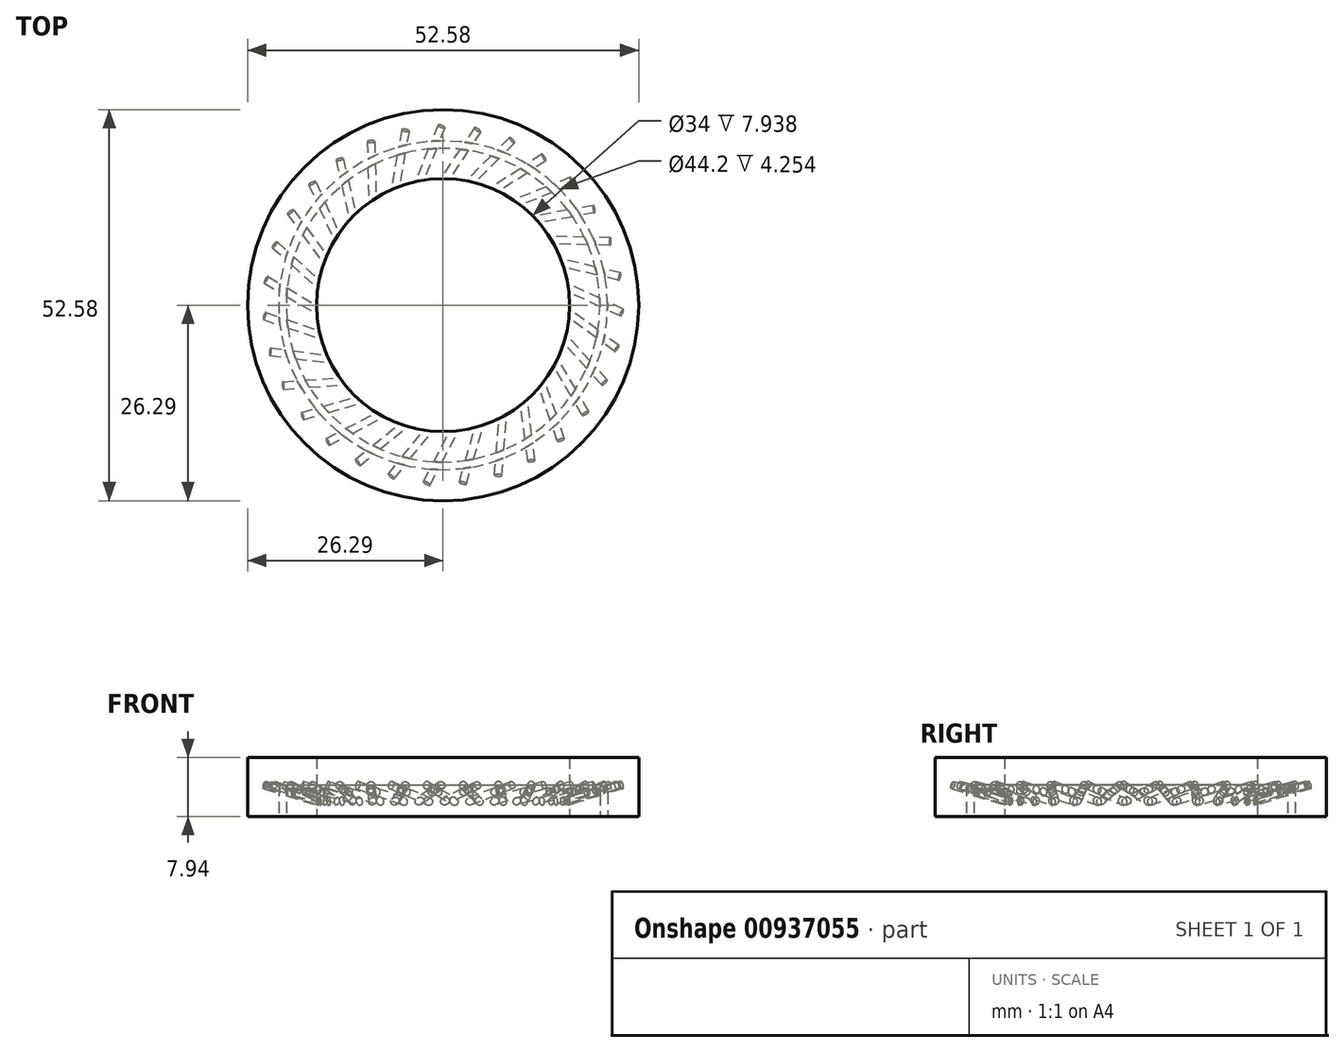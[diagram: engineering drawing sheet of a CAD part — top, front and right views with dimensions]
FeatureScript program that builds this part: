
annotation { "Feature Type Name" : "Feature", "Feature Type Description" : "" }
export const myFeature = defineFeature(function(context is Context, id is Id, definition is map)
    precondition{}
    {
        {
            var Q0;
            Q0=qCreatedBy(makeId("Top.planeOp"),FACE);
            var sketch = newSketch(context, id + "F0", { "sketchPlane" : qUnion([Q0])});
            skCircle(sketch, "E0", {"center": v(0, 0) * mm, "radius": 26.29 * mm});
            skSolve(sketch);
        }
        {
            var Q0;
            Q0=makeQuery(id+"F0.imprint","IMPRINT",FACE,{"disambiguationData":[TD([[makeQuery(id+"F0.imprint","IMPRINT",EDGE,{"derivedFrom":sQuery(id+"F0.wireOp",EDGE,"E0")}),1.0]])]});
            extrude(context, id + "F1", {"entities" : qUnion([Q0]), "depth" : 7.94 * mm, "offsetDistance" : 25.4 * mm});
        }
        {
            var Q0;
            Q0=qCreatedBy(makeId("Top.planeOp"),FACE);
            var sketch = newSketch(context, id + "F2", { "sketchPlane" : qUnion([Q0])});
            skCircle(sketch, "E1", {"center": v(0, 0) * mm, "radius": 17 * mm});
            skSolve(sketch);
        }
        {
            var Q0;
            Q0=qSketchRegion(id+"F2",true);
            extrude(context, id + "F3", {"entities" : qUnion([Q0]), "operationType" : NewBodyOperationType.REMOVE, "depth" : 7.94 * mm, "offsetDistance" : 25.4 * mm});
        }
        {
            var Q0;
            Q0=qCreatedBy(makeId("Right.planeOp"),FACE);
            var sketch = newSketch(context, id + "F4", { "sketchPlane" : qUnion([Q0])});
            skLineSegment(sketch, "E2", {"start": v(0, 0) * mm, "end": v(0, 143.33) * mm});
            skLineSegment(sketch, "E3", {"start": v(-8.9, 0) * mm, "end": v(-8.9, 70.97) * mm});
            skSolve(sketch);
        }
        {
            var Q0;
            Q0=qCreatedBy(makeId("Top.planeOp"),FACE);
            var sketch = newSketch(context, id + "F5", { "sketchPlane" : qUnion([Q0])});
            skLineSegment(sketch, "E4", {"start": v(0, 0) * mm, "end": v(29.86, 0) * mm});
            skSolve(sketch);
        }
        {
            var Q0;
            Q0=qCreatedBy(makeId("Right.planeOp"),FACE);
            var sketch = newSketch(context, id + "F6", { "sketchPlane" : qUnion([Q0])});
            skCircle(sketch, "E5", {"center": v(0, 54.1) * mm, "radius": 0.5 * mm});
            skSolve(sketch);
        }
        {
            var Q0;
            Q0=makeQuery(id+"F6.imprint","IMPRINT",FACE,{"disambiguationData":[TD([[makeQuery(id+"F6.imprint","IMPRINT",EDGE,{"derivedFrom":sQuery(id+"F6.wireOp",EDGE,"E5")}),1.0]])]});
            extrude(context, id + "F7", {"entities" : qUnion([Q0]), "depth" : 28.57 * mm, "offsetDistance" : 25.4 * mm});
        }
        {
            var Q0;
            Q0=makeQuery(id+"F7.opExtrude","SWEPT_BODY",BODY,{"disambiguationData":[OSD([sQuery(id+"F6.wireOp",EDGE,"E5")])]});
            var Q1;
            Q1=sQuery(id+"F4.wireOp",EDGE,"E2");
            transform(context, id + "F8", {"entities" : qUnion([Q0]), "transformType" : TransformType.ROTATION, "transformAxis" : qUnion([Q1]), "angle" : 20 * degree, "makeCopy" : false});
        }
        {
            var Q0;
            Q0=makeQuery(id+"F7.opExtrude","SWEPT_BODY",BODY,{"disambiguationData":[OSD([sQuery(id+"F6.wireOp",EDGE,"E5")])]});
            transform(context, id + "F9", {"entities" : qUnion([Q0]), "transformType" : TransformType.TRANSLATION_3D, "dx" : 0 * mm, "dy" : 0 * mm, "dz" : -59.18 * mm, "makeCopy" : false});
        }
        {
            var Q0;
            Q0=makeQuery(id+"F7.opExtrude","SWEPT_BODY",BODY,{"disambiguationData":[OSD([sQuery(id+"F6.wireOp",EDGE,"E5")])]});
            var Q1;
            Q1=sQuery(id+"F5.wireOp",EDGE,"E4");
            var Q2;
            Q2=sQuery(id+"F5.wireOp",EDGE,"E4");
            transform(context, id + "F10", {"entities" : qUnion([Q0]), "transformType" : TransformType.ROTATION, "transformAxis" : qUnion([Q2]), "angle" : 50 * degree, "makeCopy" : false});
        }
        {
            var Q0;
            Q0=makeQuery(id+"F7.opExtrude","SWEPT_BODY",BODY,{"disambiguationData":[OSD([sQuery(id+"F6.wireOp",EDGE,"E5")])]});
            var Q1;
            Q1=sQuery(id+"F4.wireOp",EDGE,"E2");
            var Q2;
            Q2=sQuery(id+"F4.wireOp",EDGE,"E3");
            transform(context, id + "F11", {"entities" : qUnion([Q0]), "transformType" : TransformType.ROTATION, "transformAxis" : qUnion([Q2]), "angle" : 55 * degree, "makeCopy" : false});
        }
        {
            var Q0;
            Q0=makeQuery(id+"F7.opExtrude","SWEPT_BODY",BODY,{"disambiguationData":[OSD([sQuery(id+"F6.wireOp",EDGE,"E5")])]});
            var Q1;
            Q1=sQuery(id+"F4.wireOp",EDGE,"E2");
            circularPattern(context, id + "F12", {"entities" : qUnion([Q0]), "axis" : qUnion([Q1]), "angle" : 360 * degree, "instanceCount" : 31, "equalSpace" : true});
        }
        {
            var Q0;
            Q0=makeQuery(id+"F7.opExtrude","SWEPT_BODY",BODY,{"disambiguationData":[OSD([sQuery(id+"F6.wireOp",EDGE,"E5")])]});
            var Q1;
            Q1=makeQuery(id+"F12.opPattern","COPY",BODY,{"derivedFrom":makeQuery(id+"F7.opExtrude","SWEPT_BODY",BODY,{"disambiguationData":[OSD([sQuery(id+"F6.wireOp",EDGE,"E5")])]}),"instanceName":"14"});
            var Q2;
            Q2=makeQuery(id+"F1.opExtrude","SWEPT_BODY",BODY,{"disambiguationData":[OSD([sQuery(id+"F0.wireOp",EDGE,"E0")])]});
            booleanBodies(context, id + "F13", {"operationType" : BooleanOperationType.SUBTRACTION, "tools" : qUnion([Q0, Q1]), "targets" : qUnion([Q2])});
        }
        {
            var Q0;
            Q0=makeQuery(id+"F12.opPattern","COPY",BODY,{"derivedFrom":makeQuery(id+"F7.opExtrude","SWEPT_BODY",BODY,{"disambiguationData":[OSD([sQuery(id+"F6.wireOp",EDGE,"E5")])]}),"instanceName":"30"});
            var Q1;
            Q1=makeQuery(id+"F12.opPattern","COPY",BODY,{"derivedFrom":makeQuery(id+"F7.opExtrude","SWEPT_BODY",BODY,{"disambiguationData":[OSD([sQuery(id+"F6.wireOp",EDGE,"E5")])]}),"instanceName":"28"});
            var Q2;
            Q2=makeQuery(id+"F12.opPattern","COPY",BODY,{"derivedFrom":makeQuery(id+"F7.opExtrude","SWEPT_BODY",BODY,{"disambiguationData":[OSD([sQuery(id+"F6.wireOp",EDGE,"E5")])]}),"instanceName":"26"});
            var Q3;
            Q3=makeQuery(id+"F12.opPattern","COPY",BODY,{"derivedFrom":makeQuery(id+"F7.opExtrude","SWEPT_BODY",BODY,{"disambiguationData":[OSD([sQuery(id+"F6.wireOp",EDGE,"E5")])]}),"instanceName":"24"});
            var Q4;
            Q4=makeQuery(id+"F12.opPattern","COPY",BODY,{"derivedFrom":makeQuery(id+"F7.opExtrude","SWEPT_BODY",BODY,{"disambiguationData":[OSD([sQuery(id+"F6.wireOp",EDGE,"E5")])]}),"instanceName":"22"});
            var Q5;
            Q5=makeQuery(id+"F1.opExtrude","SWEPT_BODY",BODY,{"disambiguationData":[OSD([sQuery(id+"F0.wireOp",EDGE,"E0")])]});
            booleanBodies(context, id + "F14", {"operationType" : BooleanOperationType.SUBTRACTION, "tools" : qUnion([Q0, Q1, Q2, Q3, Q4]), "targets" : qUnion([Q5])});
        }
        {
            var Q0;
            Q0=makeQuery(id+"F12.opPattern","COPY",BODY,{"derivedFrom":makeQuery(id+"F7.opExtrude","SWEPT_BODY",BODY,{"disambiguationData":[OSD([sQuery(id+"F6.wireOp",EDGE,"E5")])]}),"instanceName":"20"});
            var Q1;
            Q1=makeQuery(id+"F12.opPattern","COPY",BODY,{"derivedFrom":makeQuery(id+"F7.opExtrude","SWEPT_BODY",BODY,{"disambiguationData":[OSD([sQuery(id+"F6.wireOp",EDGE,"E5")])]}),"instanceName":"18"});
            var Q2;
            Q2=makeQuery(id+"F12.opPattern","COPY",BODY,{"derivedFrom":makeQuery(id+"F7.opExtrude","SWEPT_BODY",BODY,{"disambiguationData":[OSD([sQuery(id+"F6.wireOp",EDGE,"E5")])]}),"instanceName":"16"});
            var Q3;
            Q3=makeQuery(id+"F12.opPattern","COPY",BODY,{"derivedFrom":makeQuery(id+"F7.opExtrude","SWEPT_BODY",BODY,{"disambiguationData":[OSD([sQuery(id+"F6.wireOp",EDGE,"E5")])]}),"instanceName":"13"});
            var Q4;
            Q4=makeQuery(id+"F12.opPattern","COPY",BODY,{"derivedFrom":makeQuery(id+"F7.opExtrude","SWEPT_BODY",BODY,{"disambiguationData":[OSD([sQuery(id+"F6.wireOp",EDGE,"E5")])]}),"instanceName":"11"});
            var Q5;
            Q5=makeQuery(id+"F12.opPattern","COPY",BODY,{"derivedFrom":makeQuery(id+"F7.opExtrude","SWEPT_BODY",BODY,{"disambiguationData":[OSD([sQuery(id+"F6.wireOp",EDGE,"E5")])]}),"instanceName":"9"});
            var Q6;
            Q6=makeQuery(id+"F12.opPattern","COPY",BODY,{"derivedFrom":makeQuery(id+"F7.opExtrude","SWEPT_BODY",BODY,{"disambiguationData":[OSD([sQuery(id+"F6.wireOp",EDGE,"E5")])]}),"instanceName":"7"});
            var Q7;
            Q7=makeQuery(id+"F12.opPattern","COPY",BODY,{"derivedFrom":makeQuery(id+"F7.opExtrude","SWEPT_BODY",BODY,{"disambiguationData":[OSD([sQuery(id+"F6.wireOp",EDGE,"E5")])]}),"instanceName":"5"});
            var Q8;
            Q8=makeQuery(id+"F12.opPattern","COPY",BODY,{"derivedFrom":makeQuery(id+"F7.opExtrude","SWEPT_BODY",BODY,{"disambiguationData":[OSD([sQuery(id+"F6.wireOp",EDGE,"E5")])]}),"instanceName":"3"});
            var Q9;
            Q9=makeQuery(id+"F12.opPattern","COPY",BODY,{"derivedFrom":makeQuery(id+"F7.opExtrude","SWEPT_BODY",BODY,{"disambiguationData":[OSD([sQuery(id+"F6.wireOp",EDGE,"E5")])]}),"instanceName":"1"});
            var Q10;
            Q10=makeQuery(id+"F1.opExtrude","SWEPT_BODY",BODY,{"disambiguationData":[OSD([sQuery(id+"F0.wireOp",EDGE,"E0")])]});
            booleanBodies(context, id + "F15", {"operationType" : BooleanOperationType.SUBTRACTION, "tools" : qUnion([Q0, Q1, Q2, Q3, Q4, Q5, Q6, Q7, Q8, Q9]), "targets" : qUnion([Q10])});
        }
        {
            var Q0;
            Q0=makeQuery(id+"F12.opPattern","COPY",BODY,{"derivedFrom":makeQuery(id+"F7.opExtrude","SWEPT_BODY",BODY,{"disambiguationData":[OSD([sQuery(id+"F6.wireOp",EDGE,"E5")])]}),"instanceName":"29"});
            var Q1;
            Q1=makeQuery(id+"F12.opPattern","COPY",BODY,{"derivedFrom":makeQuery(id+"F7.opExtrude","SWEPT_BODY",BODY,{"disambiguationData":[OSD([sQuery(id+"F6.wireOp",EDGE,"E5")])]}),"instanceName":"27"});
            var Q2;
            Q2=makeQuery(id+"F12.opPattern","COPY",BODY,{"derivedFrom":makeQuery(id+"F7.opExtrude","SWEPT_BODY",BODY,{"disambiguationData":[OSD([sQuery(id+"F6.wireOp",EDGE,"E5")])]}),"instanceName":"25"});
            var Q3;
            Q3=makeQuery(id+"F12.opPattern","COPY",BODY,{"derivedFrom":makeQuery(id+"F7.opExtrude","SWEPT_BODY",BODY,{"disambiguationData":[OSD([sQuery(id+"F6.wireOp",EDGE,"E5")])]}),"instanceName":"23"});
            var Q4;
            Q4=makeQuery(id+"F12.opPattern","COPY",BODY,{"derivedFrom":makeQuery(id+"F7.opExtrude","SWEPT_BODY",BODY,{"disambiguationData":[OSD([sQuery(id+"F6.wireOp",EDGE,"E5")])]}),"instanceName":"21"});
            var Q5;
            Q5=makeQuery(id+"F12.opPattern","COPY",BODY,{"derivedFrom":makeQuery(id+"F7.opExtrude","SWEPT_BODY",BODY,{"disambiguationData":[OSD([sQuery(id+"F6.wireOp",EDGE,"E5")])]}),"instanceName":"19"});
            var Q6;
            Q6=makeQuery(id+"F12.opPattern","COPY",BODY,{"derivedFrom":makeQuery(id+"F7.opExtrude","SWEPT_BODY",BODY,{"disambiguationData":[OSD([sQuery(id+"F6.wireOp",EDGE,"E5")])]}),"instanceName":"17"});
            var Q7;
            Q7=makeQuery(id+"F12.opPattern","COPY",BODY,{"derivedFrom":makeQuery(id+"F7.opExtrude","SWEPT_BODY",BODY,{"disambiguationData":[OSD([sQuery(id+"F6.wireOp",EDGE,"E5")])]}),"instanceName":"15"});
            var Q8;
            Q8=makeQuery(id+"F12.opPattern","COPY",BODY,{"derivedFrom":makeQuery(id+"F7.opExtrude","SWEPT_BODY",BODY,{"disambiguationData":[OSD([sQuery(id+"F6.wireOp",EDGE,"E5")])]}),"instanceName":"12"});
            var Q9;
            Q9=makeQuery(id+"F12.opPattern","COPY",BODY,{"derivedFrom":makeQuery(id+"F7.opExtrude","SWEPT_BODY",BODY,{"disambiguationData":[OSD([sQuery(id+"F6.wireOp",EDGE,"E5")])]}),"instanceName":"10"});
            var Q10;
            Q10=makeQuery(id+"F12.opPattern","COPY",BODY,{"derivedFrom":makeQuery(id+"F7.opExtrude","SWEPT_BODY",BODY,{"disambiguationData":[OSD([sQuery(id+"F6.wireOp",EDGE,"E5")])]}),"instanceName":"8"});
            var Q11;
            Q11=makeQuery(id+"F12.opPattern","COPY",BODY,{"derivedFrom":makeQuery(id+"F7.opExtrude","SWEPT_BODY",BODY,{"disambiguationData":[OSD([sQuery(id+"F6.wireOp",EDGE,"E5")])]}),"instanceName":"6"});
            var Q12;
            Q12=makeQuery(id+"F12.opPattern","COPY",BODY,{"derivedFrom":makeQuery(id+"F7.opExtrude","SWEPT_BODY",BODY,{"disambiguationData":[OSD([sQuery(id+"F6.wireOp",EDGE,"E5")])]}),"instanceName":"4"});
            var Q13;
            Q13=makeQuery(id+"F12.opPattern","COPY",BODY,{"derivedFrom":makeQuery(id+"F7.opExtrude","SWEPT_BODY",BODY,{"disambiguationData":[OSD([sQuery(id+"F6.wireOp",EDGE,"E5")])]}),"instanceName":"2"});
            var Q14;
            Q14=makeQuery(id+"F1.opExtrude","SWEPT_BODY",BODY,{"disambiguationData":[OSD([sQuery(id+"F0.wireOp",EDGE,"E0")])]});
            booleanBodies(context, id + "F16", {"operationType" : BooleanOperationType.SUBTRACTION, "tools" : qUnion([Q0, Q1, Q2, Q3, Q4, Q5, Q6, Q7, Q8, Q9, Q10, Q11, Q12, Q13]), "targets" : qUnion([Q14])});
        }
        {
            var Q0;
            Q0=makeQuery(id+"F1.opExtrude","CAP_FACE",FACE,{"disambiguationData":[OSD([sQuery(id+"F0.wireOp",EDGE,"E0")])],"isStart":true});
            var sketch = newSketch(context, id + "F17", { "sketchPlane" : qUnion([Q0])});
            skCircle(sketch, "E6", {"center": v(0, 0) * mm, "radius": 21.08 * mm});
            skCircle(sketch, "E7", {"center": v(0, 0) * mm, "radius": 22.1 * mm});
            skSolve(sketch);
        }
        {
            var Q0;
            Q0=makeQuery(id+"F17.imprint","IMPRINT",FACE,{"disambiguationData":[TD([[makeQuery(id+"F17.imprint","IMPRINT",EDGE,{"derivedFrom":sQuery(id+"F17.wireOp",EDGE,"E6")}),-1.0]])]});
            var Q1;
            Q1=sQuery(id+"F17.wireOp",EDGE,"E6");
            var Q2;
            Q2=sQuery(id+"F17.wireOp",EDGE,"E7");
            var Q3;
            Q3=makeQuery(id+"FpzXc9LI6QraRG2_1.boolean.opBoolean","COPY",FACE,{"derivedFrom":makeQuery(id+"FpzXc9LI6QraRG2_1.opExtrude","CAP_FACE",FACE,{"disambiguationData":[OSD([sQuery(id+"F2.wireOp",EDGE,"E1"),sQuery(id+"F7YHOLRjezt0luX_1.wireOp",EDGE,"R3z8U0Nj-wMPZ-Womr-ymbY-DUQqCDqGNu0j")])],"isStart":false})});
            extrude(context, id + "F18", {"entities" : qUnion([Q0]), "operationType" : NewBodyOperationType.REMOVE, "surfaceEntities" : qUnion([Q1, Q2]), "oppositeDirection" : true, "depth" : 4.25 * mm, "endBoundEntityFace" : qUnion([Q3]), "offsetDistance" : 12.7 * mm, "offsetOppositeDirection" : true});
        }
    });
